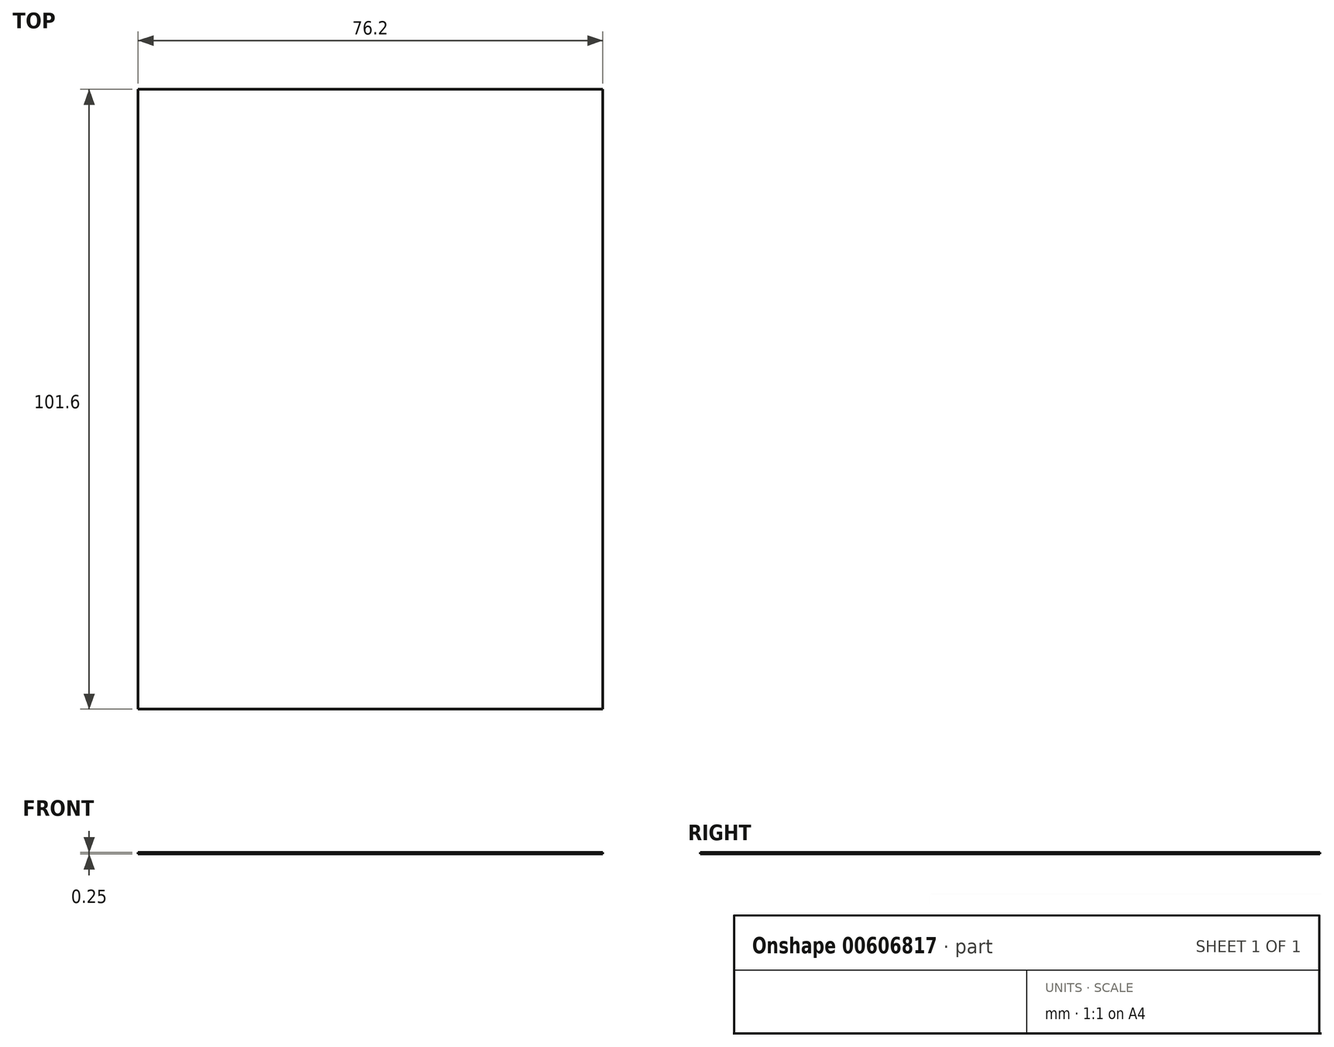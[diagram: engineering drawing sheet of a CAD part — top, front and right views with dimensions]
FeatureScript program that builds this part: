
annotation { "Feature Type Name" : "Feature", "Feature Type Description" : "" }
export const myFeature = defineFeature(function(context is Context, id is Id, definition is map)
    precondition{}
    {
        {
            var Q0;
            Q0=qCreatedBy(makeId("Top.planeOp"),FACE);
            var sketch = newSketch(context, id + "F0", { "sketchPlane" : qUnion([Q0])});
            skLineSegment(sketch, "E0.top", {"start": v(38.1, -63.5) * mm, "end": v(-38.1, -63.5) * mm});
            skLineSegment(sketch, "E0.left", {"start": v(38.1, 38.1) * mm, "end": v(38.1, -63.5) * mm});
            skLineSegment(sketch, "E0.right", {"start": v(-38.1, 38.1) * mm, "end": v(-38.1, -63.5) * mm});
            skPoint(sketch, "E0.middle", {"position": v(0, 0) * mm});
            skLineSegment(sketch, "E1.top", {"start": v(-38.1, 38.1) * mm, "end": v(38.1, 38.1) * mm});
            skPoint(sketch, "E0.bottom.end.orphan", {"position": v(-38.1, 63.5) * mm});
            skPoint(sketch, "E2.orphan", {"position": v(38.1, 63.5) * mm});
            skSolve(sketch);
        }
        {
            var Q0;
            Q0=makeQuery(id+"F0.imprint","IMPRINT",FACE,{"disambiguationData":[TD([[makeQuery(id+"F0.imprint","IMPRINT",EDGE,{"derivedFrom":sQuery(id+"F0.wireOp",EDGE,"E0.top")}),-1.0]])]});
            extrude(context, id + "F1", {"entities" : qUnion([Q0]), "depth" : 0.25 * mm, "offsetDistance" : 25.4 * mm});
        }
    });
